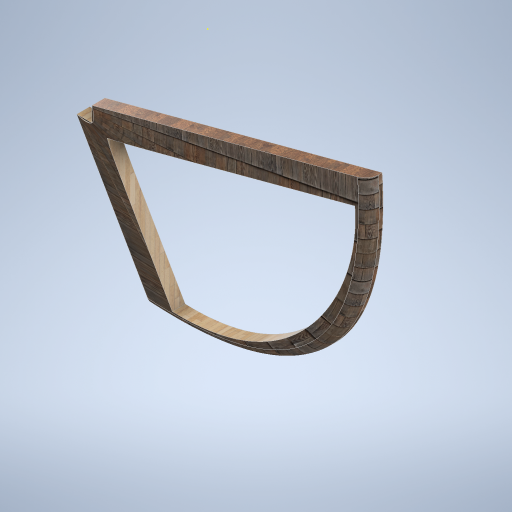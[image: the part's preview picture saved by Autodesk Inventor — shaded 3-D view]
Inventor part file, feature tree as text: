
AUTODESK INVENTOR PART (.ipt)
format: ipt  version: 2024.2 (Build 282272000, 272)  size: 477,696 bytes
history: native  units: mm
features: sketch x13, plane x8, extrude x3, projected_geometry x3, other x2, loft x1, fillet x1
ambient origin geometry x8: Origin, YZ Plane, XZ Plane, XY Plane, X Axis, Y Axis, Z Axis, Center Point
bodies: Solid1 (feature_tree)
feature tree (31):
  sketch  "Sketch1"  dims[d0=175.0mm d1=150.0mm]
  plane  "Work Plane2"
  sketch  "Sketch2"  dims[d2=-2349.0mm d3=12.217305mm]
  plane  "Work Plane3"
  extrude  "Extrusion1"  Depth=150.0mm
  sketch  "Sketch4"  dims[d7=175.0mm d8=150.0mm d9=2349.0mm]
  plane  "Work Plane4"
  sketch  "Sketch5"  dims[d11=12.217305mm]
  plane  "Work Plane5"
  extrude  "Extrusion2"  Depth=12.217305mm
  plane  "Work Plane6"
  sketch  "Sketch7"  dims[d14=0.0mm]
  plane  "Work Plane7"
  plane  "Work Plane8"
  sketch  "Sketch9"  dims[d16=90.0deg]
  sketch  "Sketch8"  dims[d15=2000.0mm]
  sketch  "Sketch10"  dims[d17=150.0mm]
  sketch  "Sketch11"  dims[d18=0.0mm d19=90.0deg]
  loft  "Loft1"
  sketch  "Sketch12"  dims[d20=0.0mm d21=90.0deg]
  extrude  "Extrusion3"  Depth=150.0mm
  fillet  "Fillet1"  Radius=2349.0mm
  sketch  "Sketch14"  dims[d22=0.0mm d23=90.0deg d24=120.0mm d25=120.0mm d26=120.0mm d27=120.0mm d28=120.0mm d29=120.0mm d30=2000.0mm d31=0.0mm d32=0.0mm d33=150.0mm]
  plane  "Work Plane1"
  sketch  "Sketch3"  dims[d4=12.217305mm d5=175.0mm d6=0.0mm]
  sketch  "Sketch6"  dims[d12=175.0mm d13=0.0mm]
  projected_geometry  "Projected Loop1"
  projected_geometry  "Projected Loop2"
  other  "Edges1"
  other  "Edges2"
  projected_geometry  "Projected Loop3"
